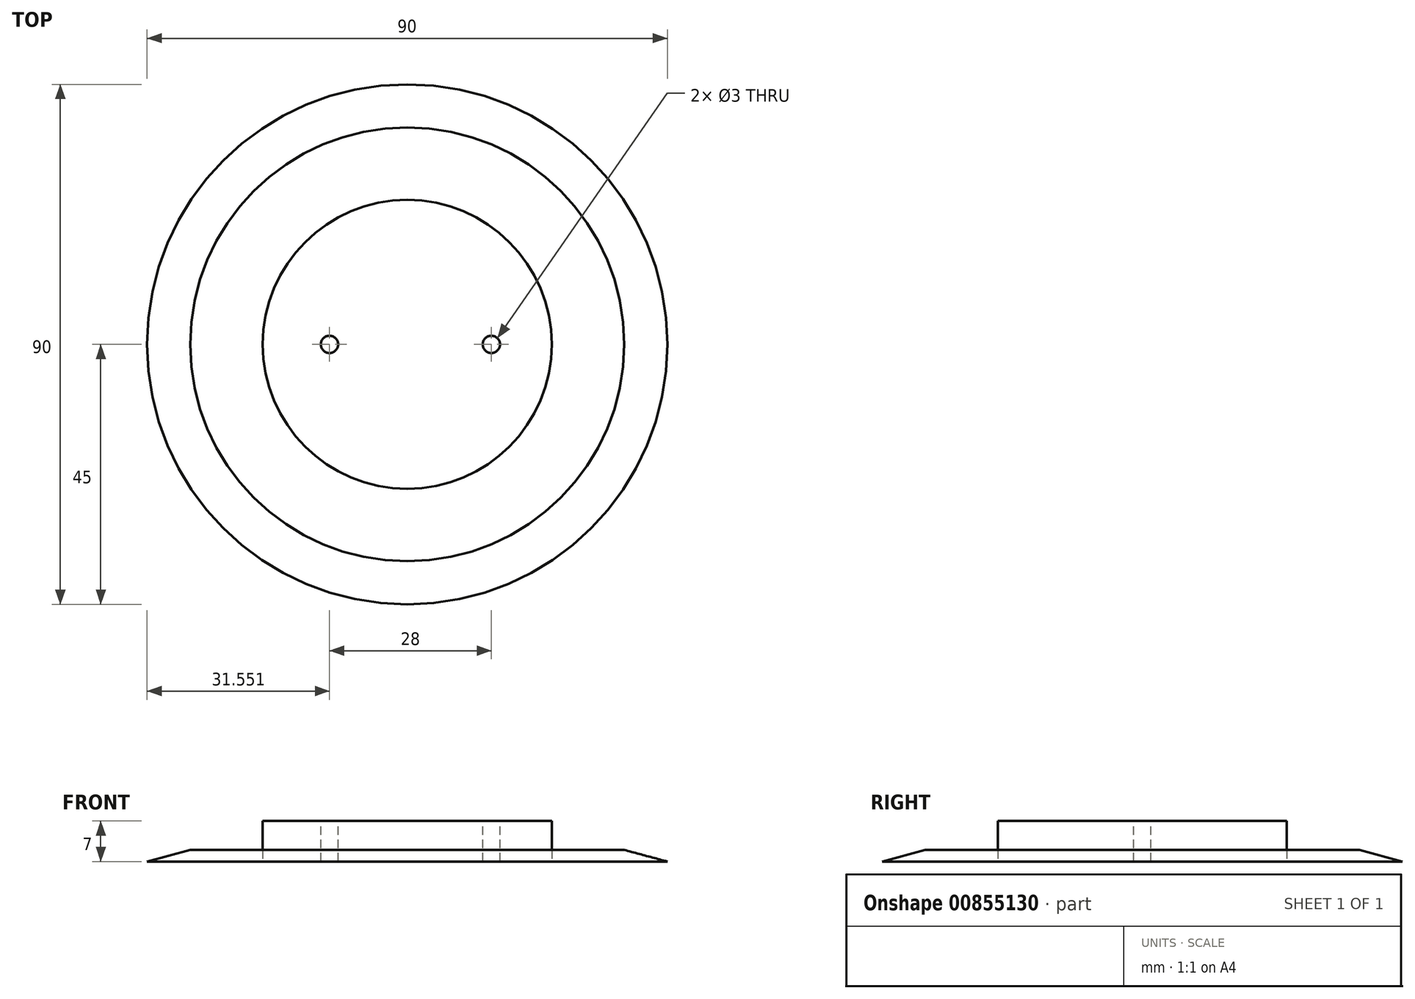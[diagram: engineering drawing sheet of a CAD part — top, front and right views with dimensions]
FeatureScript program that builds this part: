
annotation { "Feature Type Name" : "Feature", "Feature Type Description" : "" }
export const myFeature = defineFeature(function(context is Context, id is Id, definition is map)
    precondition{}
    {
        {
            var Q0;
            Q0=qCreatedBy(makeId("Top.planeOp"),FACE);
            var sketch = newSketch(context, id + "F0", { "sketchPlane" : qUnion([Q0])});
            skCircle(sketch, "E0", {"center": v(0, 0) * mm, "radius": 25 * mm});
            skSolve(sketch);
        }
        {
            var Q0;
            Q0=makeQuery(id+"F0.imprint","IMPRINT",FACE,{"disambiguationData":[TD([[makeQuery(id+"F0.imprint","IMPRINT",EDGE,{"derivedFrom":sQuery(id+"F0.wireOp",EDGE,"E0")}),1.0]])]});
            extrude(context, id + "F1", {"entities" : qUnion([Q0]), "depth" : 7 * mm, "offsetDistance" : 25 * mm});
        }
        {
            var Q0;
            Q0=makeQuery(id+"F1.opExtrude","CAP_FACE",FACE,{"disambiguationData":[OSD([sQuery(id+"F0.wireOp",EDGE,"E0")])],"isStart":false});
            var sketch = newSketch(context, id + "F2", { "sketchPlane" : qUnion([Q0])});
            skPoint(sketch, "E1", {"position": v(-13.45, 0) * mm});
            skPoint(sketch, "E2", {"position": v(14.55, 0) * mm});
            skSolve(sketch);
        }
        {
            var Q0;
            Q0=sQuery(id+"F2.wireOp",VERTEX,"E1");
            var Q1;
            Q1=sQuery(id+"F2.wireOp",VERTEX,"E2");
            var Q2;
            Q2=makeQuery(id+"F1.opExtrude","SWEPT_BODY",BODY,{"disambiguationData":[OSD([sQuery(id+"F0.wireOp",EDGE,"E0")])]});
            hole(context, id + "F3", {"style" : HoleStyle.SIMPLE, "endStyle" : HoleEndStyle.THROUGH, "holeDiameter" : 3 * mm, "majorDiameter" : 5 * mm, "isTappedThrough" : true, "tappedDepth" : 12 * mm, "tapClearance" : 3, "locations" : qUnion([Q0, Q1]), "scope" : qUnion([Q2])});
        }
        {
            var Q0;
            Q0=qCreatedBy(makeId("Top.planeOp"),FACE);
            var sketch = newSketch(context, id + "F4", { "sketchPlane" : qUnion([Q0])});
            skCircle(sketch, "E3", {"center": v(0, 0) * mm, "radius": 45 * mm});
            skSolve(sketch);
        }
        {
            var Q0;
            Q0=makeQuery(id+"F4.imprint","IMPRINT",FACE,{"disambiguationData":[TD([[makeQuery(id+"F4.imprint","IMPRINT",EDGE,{"derivedFrom":sQuery(id+"F4.wireOp",EDGE,"E3")}),1.0]])]});
            extrude(context, id + "F5", {"entities" : qUnion([Q0]), "depth" : 2 * mm, "offsetDistance" : 25 * mm, "hasDraft" : true, "draftAngle" : 75 * degree, "draftPullDirection" : true});
        }
    });
